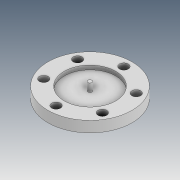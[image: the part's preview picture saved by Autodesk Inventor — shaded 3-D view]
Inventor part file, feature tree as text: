
AUTODESK INVENTOR PART (.ipt)
format: ipt  version: 2020 (Build 240168000, 168)  size: 133,632 bytes
history: native  units: mm
features: sketch x2, revolve x1, extrude x1, pattern_circular x1, projected_geometry x1
ambient origin geometry x8: Origin, YZ Plane, XZ Plane, XY Plane, X Axis, Y Axis, Z Axis, Center Point
bodies: Solid1 (feature_tree)
feature tree (6):
  revolve  "Revolution1"  [1 undecoded]
  extrude  "Extrusion1"  Depth=5.0mm
  pattern_circular  "Circular Pattern1"  Angle=45.0deg  [1 undecoded]
  sketch  "Sketch1"  dims[d1=19.0mm d2=1.5mm]
  sketch  "Sketch2"  dims[d3=1.5mm d4=5.0mm d6=45.0deg d7=10.5mm d8=2.0mm d9=12.0mm d10=5.0mm d11=90.0deg d12=6.5mm d13=10.0mm d14=0.0mm d15=60.0mm d16=360.0deg d18=6.0mm]
  projected_geometry  "Projected Loop1"
note: 2 required parameter values undecoded (feature->parameter linkage not recoverable at this tier; creation-order binding heuristic only, values carry confidence <= 0.55)